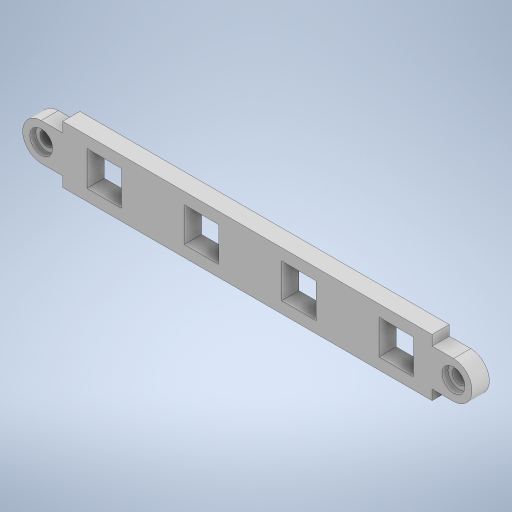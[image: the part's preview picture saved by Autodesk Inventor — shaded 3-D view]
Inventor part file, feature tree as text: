
AUTODESK INVENTOR PART (.ipt)
format: ipt  version: 2023 (Build 270158000, 158)  size: 289,792 bytes
history: native  units: mm
features: extrude x3, sketch x3, other x1
ambient origin geometry x8: Origin, YZ Plane, XZ Plane, XY Plane, X Axis, Y Axis, Z Axis, Center Point
bodies: Body1 (feature_tree)
feature tree (7):
  other  "솔리드1"
  extrude  "돌출1"  Depth=64.5mm
  extrude  "돌출2"  Depth=10.0mm
  extrude  "돌출3"  Depth=6.5mm
  sketch  "스케치1"
  sketch  "스케치2"
  sketch  "스케치3"
